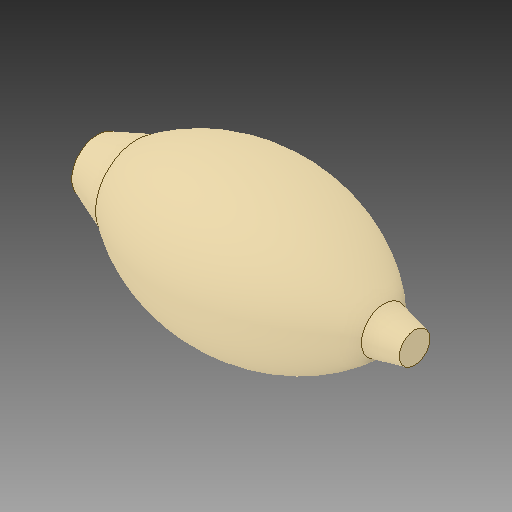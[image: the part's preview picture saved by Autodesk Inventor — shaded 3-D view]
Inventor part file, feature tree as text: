
AUTODESK INVENTOR PART (.ipt)
format: ipt  version: 2019 (Build 230136000, 136)  size: 142,336 bytes
history: native  units: mm
features: revolve x1, sketch x1
ambient origin geometry x8: Origin, YZ Plane, XZ Plane, XY Plane, X Axis, Y Axis, Z Axis, Center Point
bodies: Solid1 (feature_tree)
feature tree (2):
  revolve  "Revolution1"  [1 undecoded]
  sketch  "Sketch1"  dims[d0=202.0mm d1=63.5mm d2=33.5mm d3=18.5mm d4=32.0mm d5=21.0mm d6=25.0mm d7=12.5mm d8=90.0deg]
note: 1 required parameter value undecoded (feature->parameter linkage not recoverable at this tier; creation-order binding heuristic only, values carry confidence <= 0.55)
